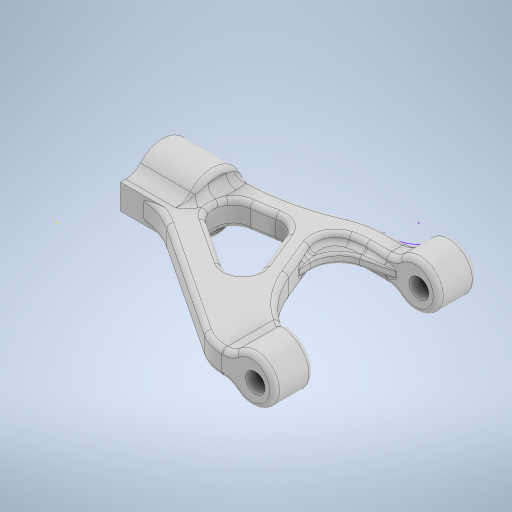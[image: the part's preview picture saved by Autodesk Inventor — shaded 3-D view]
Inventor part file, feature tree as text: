
AUTODESK INVENTOR PART (.ipt)
format: ipt  version: 2024 (Build 280153000, 153)  size: 883,200 bytes
history: native  units: in
note: dims shown in document units (in); Inventor stores cm internally (conversion verified against a paired STEP export)
features: fillet x14, sketch x11, extrude x6, projected_geometry x3, hole x2, plane x1, rib x1
ambient origin geometry x8: Origin, YZ Plane, XZ Plane, XY Plane, X Axis, Y Axis, Z Axis, Center Point
bodies: Solid1 (feature_tree)
feature tree (38):
  extrude  "Extrusion1"  Depth=0.25in TaperAngle=0.0deg
  plane  "Work Plane1"
  extrude  "Extrusion2"  Depth=0.25in TaperAngle=0.0deg
  extrude  "Extrusion3"  Depth=0.425in
  extrude  "Extrusion4"  Depth=0.158in
  fillet  "Fillet1"  Radius=1.5in
  fillet  "Fillet2"  Radius=0.163in
  extrude  "Extrusion5"  Depth=0.189in
  sketch  "Sketch6"  dims[d14=0.125in d15=0.315in d16=0.135in d17=0.5in d18=0.365in d19=0.5in d20=0.1625in d21=0.0in d22=0.154in d23=0.1278in d24=0.1625in d25=0.0in d26=0.125in d27=0.625in]
  extrude  "Extrusion6"  Depth=0.315in
  fillet  "Fillet3"  Radius=0.135in
  fillet  "Fillet4"  Radius=0.5in
  fillet  "Fillet5"  Radius=0.365in
  fillet  "Fillet6"  Radius=0.5in
  fillet  "Fillet7"  Radius=0.1625in
  fillet  "Fillet8"  Radius=0.154in
  fillet  "Fillet9"  Radius=0.1278in
  fillet  "Fillet10"  Radius=0.1625in
  fillet  "Fillet11"  Radius=0.125in
  fillet  "Fillet12"  Radius=0.625in
  hole  "Hole1"  [1 undecoded]
  hole  "Hole2"  [1 undecoded]
  rib  "Rib1"
  fillet  "Fillet13"  Radius=0.415in
  fillet  "Fillet14"  Radius=0.125in
  sketch  "Sketch11"  dims[d38=0.032in d39=0.0625in d40=0.032in d41=0.032in d42=0.032in d43=0.0625in d44=0.032in d45=0.134in d46=0.328in d47=0.75in d48=0.0625in d49=0.5635in d50=0.375in d51=0.8108in d52=0.125in d53=0.75in d54=0.375in d55=0.25in d56=0.5635in d57=0.375in d58=0.0in d59=0.1in d60=0.0625in d61=0.0in d62=0.0in d63=0.1in d64=0.1in d65=0.015in d66=0.031in]
  sketch  "Sketch1"  dims[d0=0.3in d1=0.25in d2=0.0in]
  sketch  "Sketch2"  dims[d3=0.8in d4=0.25in d5=0.0in]
  projected_geometry  "Projected Loop1"
  sketch  "Sketch3"  dims[d6=0.867in d7=0.425in]
  sketch  "Sketch4"  dims[d8=0.425in d9=0.158in d10=1.5in d11=0.163in]
  sketch  "Sketch5"  dims[d12=0.125in d13=0.189in]
  sketch  "Sketch7"  dims[d28=0.063in d29=1.0in d30=0.0in]
  sketch  "Sketch8"  dims[d31=0.375in d32=0.1575in d33=0.415in d34=0.0in d35=0.125in]
  sketch  "Sketch9"  dims[d36=0.032in]
  sketch  "Sketch10"  dims[d37=0.032in]
  projected_geometry  "Project Cut Edges1"
  projected_geometry  "Project Cut Edges2"
note: 2 required parameter values undecoded (feature->parameter linkage not recoverable at this tier; creation-order binding heuristic only, values carry confidence <= 0.55)
